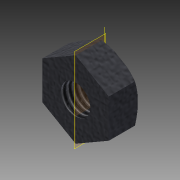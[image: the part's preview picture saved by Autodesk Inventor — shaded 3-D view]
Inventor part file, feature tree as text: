
AUTODESK INVENTOR PART (.ipt)
format: ipt  version: 2015 (Build 190159000, 159)  size: 120,832 bytes
history: native  units: mm
features: sketch x4, extrude x1, plane x1, revolve x1, hole x1, other x1, projected_geometry x1
ambient origin geometry x8: Origin, YZ Plane, XZ Plane, XY Plane, X Axis, Y Axis, Z Axis, Center Point
bodies: Solid1 (feature_tree)
feature tree (10):
  extrude  "Extrusion1"  Depth=6.5mm TaperAngle=0.0deg
  sketch  "Sketch2"  dims[d5=0.0mm d6=1.0mm]
  plane  "Work Plane2"
  revolve  "Revolution1"  [1 undecoded]
  hole  "Hole1"  [1 undecoded]
  sketch  "Sketch1"  dims[d0=15.0mm d1=6.5mm d2=0.0mm]
  other  "Work Axis1"
  sketch  "Sketch6"  dims[d7=30.0deg d8=90.0deg]
  projected_geometry  "Projected Loop2"
  sketch  "Sketch7"  dims[d9=6.647mm d10=6.0mm d11=4.0mm d12=2.0mm d13=90.0deg d14=12.75mm d15=20.594885mm]
note: 2 required parameter values undecoded (feature->parameter linkage not recoverable at this tier; creation-order binding heuristic only, values carry confidence <= 0.55)